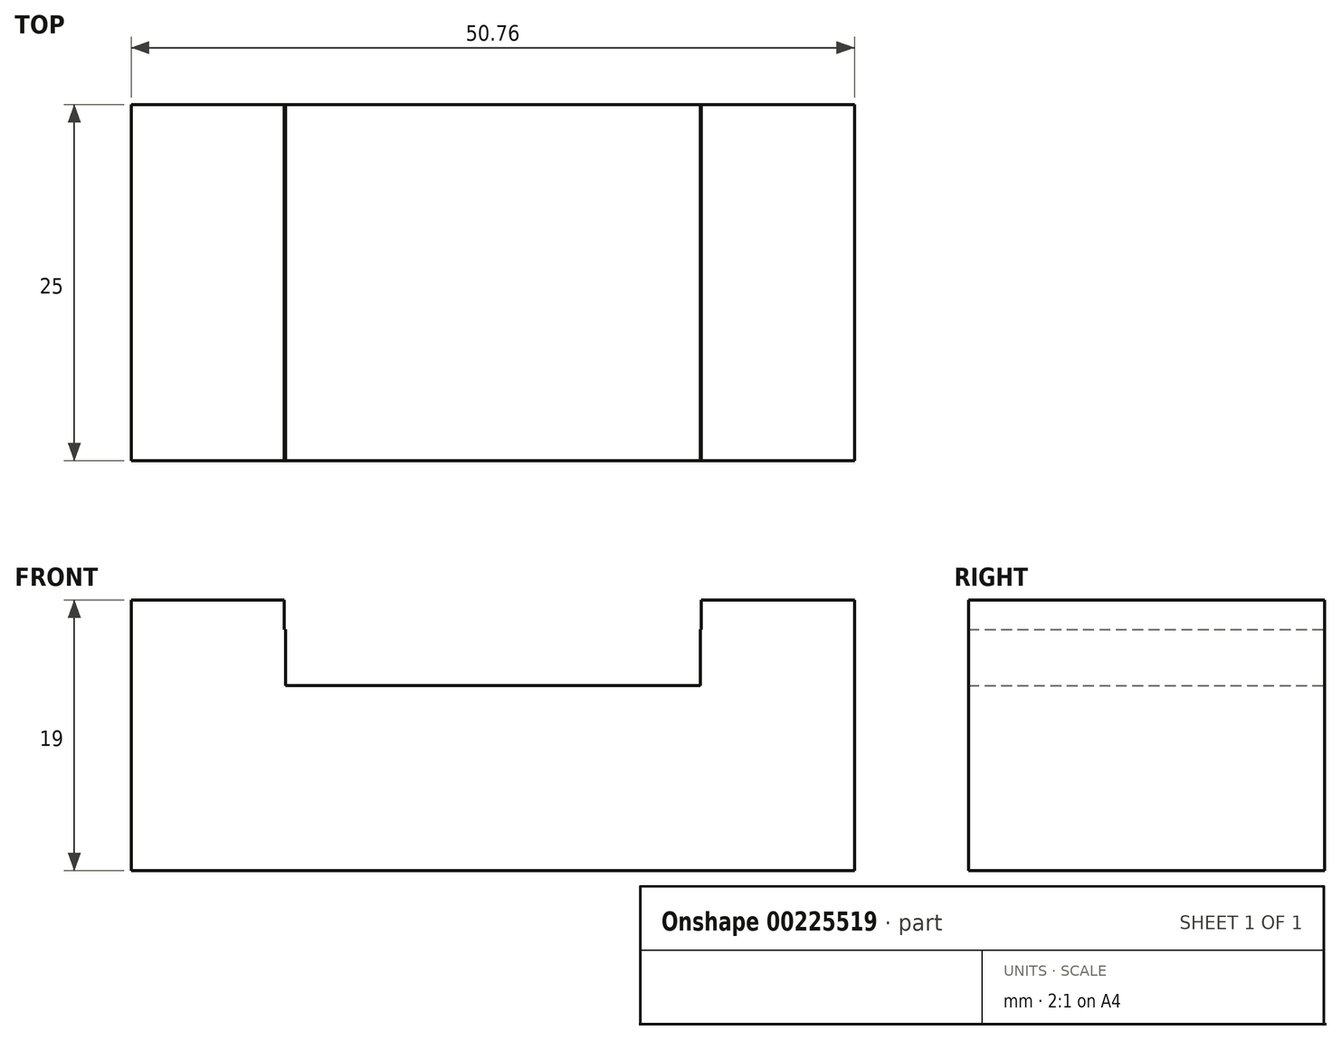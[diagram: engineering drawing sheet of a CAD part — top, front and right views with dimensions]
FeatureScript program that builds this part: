
annotation { "Feature Type Name" : "Feature", "Feature Type Description" : "" }
export const myFeature = defineFeature(function(context is Context, id is Id, definition is map)
    precondition{}
    {
        {
            var Q0;
            Q0=qCreatedBy(makeId("Front.planeOp"),FACE);
            var sketch = newSketch(context, id + "F0", { "sketchPlane" : qUnion([Q0])});
            skLineSegment(sketch, "E0", {"start": v(0, 0) * mm, "end": v(25.38, 0) * mm});
            skLineSegment(sketch, "E1", {"start": v(25.38, 0) * mm, "end": v(25.38, 19) * mm});
            skLineSegment(sketch, "E2", {"start": v(25.38, 19) * mm, "end": v(14.64, 19) * mm});
            skLineSegment(sketch, "E3", {"start": v(14.64, 19) * mm, "end": v(14.64, 16.93) * mm});
            skLineSegment(sketch, "E4", {"start": v(14.64, 16.93) * mm, "end": v(14.56, 16.93) * mm});
            skLineSegment(sketch, "E5", {"start": v(14.56, 16.93) * mm, "end": v(14.56, 13) * mm});
            skLineSegment(sketch, "E6", {"start": v(14.56, 13) * mm, "end": v(0, 13) * mm});
            skLineSegment(sketch, "E7.MirrorCS", {"start": v(0, 0) * mm, "end": v(-25.38, 0) * mm});
            skLineSegment(sketch, "E8.MirrorCS", {"start": v(-25.38, 0) * mm, "end": v(-25.38, 19) * mm});
            skLineSegment(sketch, "E9.MirrorCS", {"start": v(-25.38, 19) * mm, "end": v(-14.64, 19) * mm});
            skLineSegment(sketch, "E10.MirrorCS", {"start": v(-14.56, 16.93) * mm, "end": v(-14.56, 13) * mm});
            skLineSegment(sketch, "E11.MirrorCS", {"start": v(-14.64, 16.93) * mm, "end": v(-14.56, 16.93) * mm});
            skLineSegment(sketch, "E12.MirrorCS", {"start": v(-14.64, 19) * mm, "end": v(-14.64, 16.93) * mm});
            skLineSegment(sketch, "E13.MirrorCS", {"start": v(-14.56, 13) * mm, "end": v(0, 13) * mm});
            skSolve(sketch);
        }
        {
            var Q0;
            Q0=makeQuery(id+"F0.imprint","IMPRINT",FACE,{"disambiguationData":[TD([[makeQuery(id+"F0.imprint","IMPRINT",EDGE,{"derivedFrom":sQuery(id+"F0.wireOp",EDGE,"E0")}),1.0]])]});
            extrude(context, id + "F1", {"entities" : qUnion([Q0]), "depth" : 25 * mm});
        }
    });
